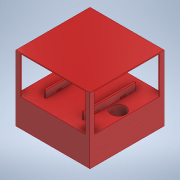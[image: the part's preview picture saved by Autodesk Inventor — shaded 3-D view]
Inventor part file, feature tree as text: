
AUTODESK INVENTOR PART (.ipt)
format: ipt  version: 2020 (Build 240168000, 168)  size: 235,008 bytes
history: native  units: mm
features: extrude x7, sketch x7, other x2, plane x2, projected_geometry x1
ambient origin geometry x8: Origin, YZ Plane, XZ Plane, XY Plane, X Axis, Y Axis, Z Axis, Center Point
bodies: Body1 (feature_tree)
feature tree (19):
  other  "Sólido1"
  extrude  "Extrusión1"  Depth=200.0mm
  extrude  "Extrusión2"  Depth=150.0mm TaperAngle=0.0deg
  other  "Eje de trabajo1"
  extrude  "Extrusión3"  Depth=60.0mm
  extrude  "Extrusión4"  Depth=60.0mm
  extrude  "Extrusión5"  Depth=280.0mm
  extrude  "Extrusión6"  Depth=10.0mm
  extrude  "Extrusión7"  Depth=97.5mm
  sketch  "Boceto1"  dims[d0=400.0mm d2=200.0mm]
  sketch  "Boceto3"  dims[d3=200.0mm d4=150.0mm d5=0.0mm]
  plane  "Plano de trabajo1"
  plane  "Plano de trabajo2"
  sketch  "Boceto4"  dims[d7=153.75mm d8=0.0mm d13=60.0mm]
  sketch  "Boceto5"  dims[d14=280.0mm d15=60.0mm]
  sketch  "Boceto6"  dims[d19=10.0mm d20=280.0mm]
  sketch  "Boceto7"  dims[d21=97.5mm d22=10.0mm]
  projected_geometry  "Contorno proyectado1"
  sketch  "Boceto8"  dims[d23=280.0mm d24=97.5mm d25=38.0mm d26=0.0mm d27=79.0mm d28=25.0mm d29=5.0mm d30=20.0mm d31=20.0mm d32=25.0mm d33=5.0mm d34=20.0mm d35=20.0mm d36=25.0mm d37=5.0mm d38=20.0mm d39=20.0mm d40=25.0mm d41=5.0mm d42=20.0mm d43=20.0mm d44=200.0mm d45=0.0mm d46=5.0mm d47=0.0mm d48=78.0mm d49=200.0mm d50=46.0mm d51=200.5mm d52=0.0mm d53=31.666667mm d54=70.0mm d55=4.0mm d56=31.666667mm d57=4.0mm d58=70.0mm d59=251.25mm d60=0.0mm]
